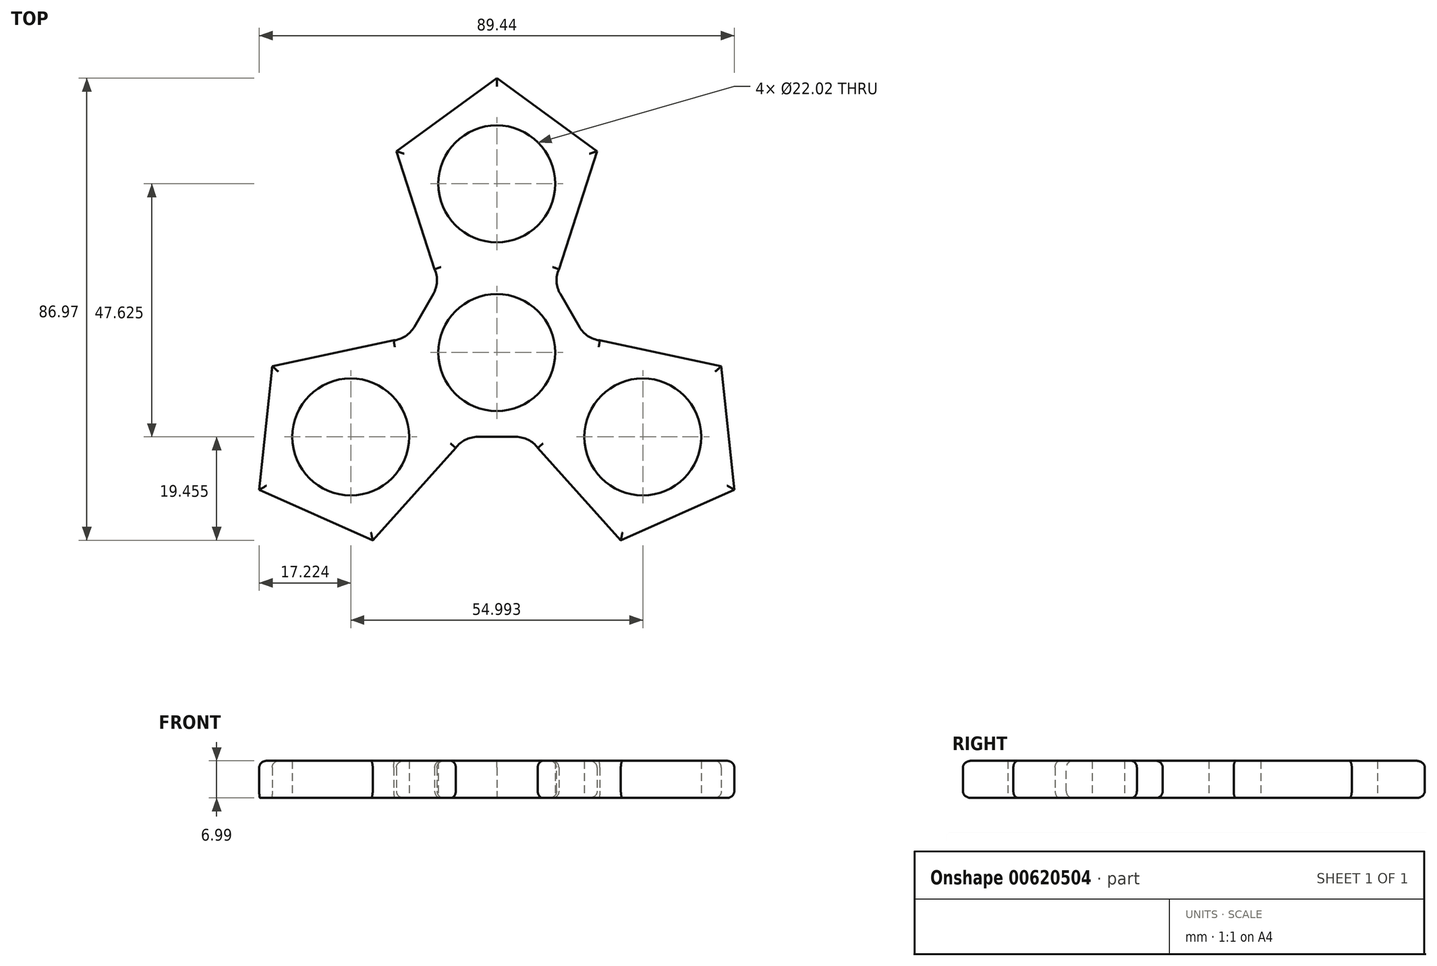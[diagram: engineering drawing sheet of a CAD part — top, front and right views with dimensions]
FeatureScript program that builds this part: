
annotation { "Feature Type Name" : "Feature", "Feature Type Description" : "" }
export const myFeature = defineFeature(function(context is Context, id is Id, definition is map)
    precondition{}
    {
        {
            var Q0;
            Q0=qCreatedBy(makeId("Top.planeOp"),FACE);
            var sketch = newSketch(context, id + "F0", { "sketchPlane" : qUnion([Q0])});
            skCircle(sketch, "E0", {"center": v(0, 0) * mm, "radius": 1.4 * mm});
            skCircle(sketch, "E1", {"center": v(0, 0) * mm, "radius": 11.01 * mm});
            skLineSegment(sketch, "E2", {"start": v(0, 0) * mm, "end": v(0, 31.75) * mm});
            skLineSegment(sketch, "E3", {"start": v(0, 0) * mm, "end": v(-27.5, -15.88) * mm});
            skLineSegment(sketch, "E4", {"start": v(0, 0) * mm, "end": v(27.5, -15.87) * mm});
            skCircle(sketch, "E5", {"center": v(0, 31.75) * mm, "radius": 11.01 * mm});
            skCircle(sketch, "E6", {"center": v(27.5, -15.87) * mm, "radius": 11.01 * mm});
            skCircle(sketch, "E7", {"center": v(-27.5, -15.88) * mm, "radius": 11.01 * mm});
            skCircle(sketch, "E8.cCircle", {"center": v(0, 31.75) * mm, "radius": 19.89 * mm, "construction": true});
            skLineSegment(sketch, "E8.0", {"start": v(0, 51.64) * mm, "end": v(18.92, 37.9) * mm});
            skLineSegment(sketch, "E8.1", {"start": v(18.92, 37.9) * mm, "end": v(11.7, 15.66) * mm});
            skLineSegment(sketch, "E8.2", {"start": v(11.7, 15.66) * mm, "end": v(-11.7, 15.66) * mm});
            skLineSegment(sketch, "E8.3", {"start": v(-11.7, 15.66) * mm, "end": v(-18.92, 37.9) * mm});
            skLineSegment(sketch, "E8.4", {"start": v(-18.92, 37.9) * mm, "end": v(0, 51.64) * mm});
            skCircle(sketch, "E9.cCircle", {"center": v(-27.5, -15.88) * mm, "radius": 19.89 * mm, "construction": true});
            skLineSegment(sketch, "E9.0", {"start": v(-19.4, 2.3) * mm, "end": v(-7.72, -17.95) * mm});
            skLineSegment(sketch, "E9.1", {"start": v(-7.72, -17.95) * mm, "end": v(-23.36, -35.33) * mm});
            skLineSegment(sketch, "E9.2", {"start": v(-23.36, -35.33) * mm, "end": v(-44.72, -25.82) * mm});
            skLineSegment(sketch, "E9.3", {"start": v(-44.72, -25.82) * mm, "end": v(-42.28, -2.57) * mm});
            skLineSegment(sketch, "E9.4", {"start": v(-42.28, -2.57) * mm, "end": v(-19.4, 2.3) * mm});
            skLineSegment(sketch, "E10", {"start": v(-27.5, -15.88) * mm, "end": v(0, 31.75) * mm});
            skLineSegment(sketch, "E11", {"start": v(0, 31.75) * mm, "end": v(27.5, -15.87) * mm});
            skLineSegment(sketch, "E12", {"start": v(27.5, -15.87) * mm, "end": v(-27.5, -15.88) * mm});
            skCircle(sketch, "E13.cCircle", {"center": v(27.5, -15.87) * mm, "radius": 19.89 * mm, "construction": true});
            skLineSegment(sketch, "E13.0", {"start": v(44.72, -25.82) * mm, "end": v(23.36, -35.33) * mm});
            skLineSegment(sketch, "E13.1", {"start": v(23.36, -35.33) * mm, "end": v(7.72, -17.95) * mm});
            skLineSegment(sketch, "E13.2", {"start": v(7.72, -17.95) * mm, "end": v(19.4, 2.3) * mm});
            skLineSegment(sketch, "E13.3", {"start": v(19.4, 2.3) * mm, "end": v(42.28, -2.57) * mm});
            skLineSegment(sketch, "E13.4", {"start": v(42.28, -2.57) * mm, "end": v(44.72, -25.82) * mm});
            skSolve(sketch);
        }
        {
            var Q0;
            Q0=makeQuery(id+"F0.imprint","IMPRINT",FACE,{"disambiguationData":[TD([[makeQuery(id+"F0.imprint","IMPRINT",EDGE,{"derivedFrom":sQuery(id+"F0.wireOp",EDGE,"E8.0")}),-1.0]])]});
            var Q1;
            {var subQ0=sQuery(id+"F0.wireOp",EDGE,"E8.2");var subQ1=sQuery(id+"F0.wireOp",EDGE,"E2");var subQ2=makeQuery(id+"F0.imprint","INTERSECT",VERTEX,{"derivedFrom":[subQ1,subQ0]});Q1=makeQuery(id+"F0.imprint","IMPRINT",FACE,{"disambiguationData":[TD([[makeQuery(id+"F0.imprint","IMPRINT",EDGE,{"disambiguationData":[TD([[subQ2,-1.0]])],"derivedFrom":subQ1}),-1.0]])]});}
            var Q2;
            {var subQ0=sQuery(id+"F0.wireOp",EDGE,"E8.2");var subQ1=sQuery(id+"F0.wireOp",EDGE,"E2");var subQ2=makeQuery(id+"F0.imprint","INTERSECT",VERTEX,{"derivedFrom":[subQ1,subQ0]});Q2=makeQuery(id+"F0.imprint","IMPRINT",FACE,{"disambiguationData":[TD([[makeQuery(id+"F0.imprint","IMPRINT",EDGE,{"disambiguationData":[TD([[subQ2,-1.0]])],"derivedFrom":subQ1}),1.0]])]});}
            var Q3;
            {var subQ1=sQuery(id+"F0.wireOp",EDGE,"E9.0");var subQ3=sQuery(id+"F0.wireOp",EDGE,"E1");var subQ4=makeQuery(id+"F0.imprint","INTERSECT",VERTEX,{"derivedFrom":[subQ3,subQ1]});Q3=makeQuery(id+"F0.imprint","IMPRINT",FACE,{"disambiguationData":[TD([[makeQuery(id+"F0.imprint","IMPRINT",EDGE,{"disambiguationData":[TD([[subQ4,1.0]])],"derivedFrom":subQ3}),-1.0]])]});}
            var Q4;
            {var subQ1=sQuery(id+"F0.wireOp",EDGE,"E9.0");var subQ3=sQuery(id+"F0.wireOp",EDGE,"E1");var subQ4=makeQuery(id+"F0.imprint","INTERSECT",VERTEX,{"derivedFrom":[subQ3,subQ1]});Q4=makeQuery(id+"F0.imprint","IMPRINT",FACE,{"disambiguationData":[TD([[makeQuery(id+"F0.imprint","IMPRINT",EDGE,{"disambiguationData":[TD([[subQ4,-1.0]])],"derivedFrom":subQ3}),-1.0]])]});}
            var Q5;
            {var subQ0=sQuery(id+"F0.wireOp",EDGE,"E9.2");Q5=makeQuery(id+"F0.imprint","IMPRINT",FACE,{"disambiguationData":[TD([[makeQuery(id+"F0.imprint","IMPRINT",EDGE,{"derivedFrom":subQ0}),-1.0]])]});}
            var Q6;
            {var subQ0=sQuery(id+"F0.wireOp",EDGE,"8ebc8318-1411-40da-9cb2-afa56d5b8b3e.0");Q6=makeQuery(id+"F0.imprint","IMPRINT",FACE,{"disambiguationData":[TD([[makeQuery(id+"F0.imprint","IMPRINT",EDGE,{"derivedFrom":subQ0}),-1.0]])]});}
            var Q7;
            {var subQ3=sQuery(id+"F0.wireOp",EDGE,"E2");var subQ10=sQuery(id+"F0.wireOp",EDGE,"E1");var subQ13=makeQuery(id+"F0.imprint","INTERSECT",VERTEX,{"derivedFrom":[subQ10,subQ3]});Q7=makeQuery(id+"F0.imprint","IMPRINT",FACE,{"disambiguationData":[TD([[makeQuery(id+"F0.imprint","IMPRINT",EDGE,{"disambiguationData":[TD([[subQ13,1.0]])],"derivedFrom":subQ10}),-1.0]])]});}
            var Q8;
            {var subQ3=sQuery(id+"F0.wireOp",EDGE,"E3");var subQ6=sQuery(id+"F0.wireOp",EDGE,"E1");var subQ10=makeQuery(id+"F0.imprint","INTERSECT",VERTEX,{"derivedFrom":[subQ6,subQ3]});Q8=makeQuery(id+"F0.imprint","IMPRINT",FACE,{"disambiguationData":[TD([[makeQuery(id+"F0.imprint","IMPRINT",EDGE,{"disambiguationData":[TD([[subQ10,-1.0]])],"derivedFrom":subQ6}),-1.0]])]});}
            var Q9;
            {var subQ0=sQuery(id+"F0.wireOp",EDGE,"E9.0");var subQ1=sQuery(id+"F0.wireOp",EDGE,"E3");var subQ2=makeQuery(id+"F0.imprint","INTERSECT",VERTEX,{"derivedFrom":[subQ1,subQ0]});Q9=makeQuery(id+"F0.imprint","IMPRINT",FACE,{"disambiguationData":[TD([[makeQuery(id+"F0.imprint","IMPRINT",EDGE,{"disambiguationData":[TD([[subQ2,-1.0]])],"derivedFrom":subQ1}),-1.0]])]});}
            var Q10;
            {var subQ0=sQuery(id+"F0.wireOp",EDGE,"E9.0");var subQ1=sQuery(id+"F0.wireOp",EDGE,"E3");var subQ2=makeQuery(id+"F0.imprint","INTERSECT",VERTEX,{"derivedFrom":[subQ1,subQ0]});Q10=makeQuery(id+"F0.imprint","IMPRINT",FACE,{"disambiguationData":[TD([[makeQuery(id+"F0.imprint","IMPRINT",EDGE,{"disambiguationData":[TD([[subQ2,-1.0]])],"derivedFrom":subQ1}),1.0]])]});}
            var Q11;
            {var subQ0=sQuery(id+"F0.wireOp",EDGE,"E13.2");var subQ1=sQuery(id+"F0.wireOp",EDGE,"E4");var subQ2=makeQuery(id+"F0.imprint","INTERSECT",VERTEX,{"derivedFrom":[subQ1,subQ0]});Q11=makeQuery(id+"F0.imprint","IMPRINT",FACE,{"disambiguationData":[TD([[makeQuery(id+"F0.imprint","IMPRINT",EDGE,{"disambiguationData":[TD([[subQ2,-1.0]])],"derivedFrom":subQ1}),-1.0]])]});}
            var Q12;
            {var subQ0=sQuery(id+"F0.wireOp",EDGE,"E13.2");var subQ1=sQuery(id+"F0.wireOp",EDGE,"E4");var subQ2=makeQuery(id+"F0.imprint","INTERSECT",VERTEX,{"derivedFrom":[subQ1,subQ0]});Q12=makeQuery(id+"F0.imprint","IMPRINT",FACE,{"disambiguationData":[TD([[makeQuery(id+"F0.imprint","IMPRINT",EDGE,{"disambiguationData":[TD([[subQ2,-1.0]])],"derivedFrom":subQ1}),1.0]])]});}
            var Q13;
            Q13=makeQuery(id+"F0.imprint","IMPRINT",FACE,{"disambiguationData":[TD([[makeQuery(id+"F0.imprint","IMPRINT",EDGE,{"derivedFrom":sQuery(id+"F0.wireOp",EDGE,"E13.0")}),-1.0]])]});
            extrude(context, id + "F1", {"entities" : qUnion([Q0, Q1, Q2, Q3, Q4, Q5, Q6, Q7, Q8, Q9, Q10, Q11, Q12, Q13]), "depth" : 7 * mm, "offsetDistance" : 25.4 * mm});
        }
        {
            var Q0;
            Q0=makeQuery(id+"F1.opExtrude","SWEPT_EDGE",EDGE,{"disambiguationData":[OSD([sQuery(id+"F0.wireOp",EDGE,"E8.2"),sQuery(id+"F0.wireOp",EDGE,"E10")])]});
            var Q1;
            Q1=makeQuery(id+"F1.opExtrude","SWEPT_EDGE",EDGE,{"disambiguationData":[OSD([sQuery(id+"F0.wireOp",EDGE,"E9.0"),sQuery(id+"F0.wireOp",EDGE,"E10")])]});
            var Q2;
            Q2=makeQuery(id+"F1.opExtrude","SWEPT_EDGE",EDGE,{"disambiguationData":[OSD([sQuery(id+"F0.wireOp",EDGE,"E9.0"),sQuery(id+"F0.wireOp",EDGE,"E12")])]});
            var Q3;
            Q3=makeQuery(id+"F1.opExtrude","SWEPT_EDGE",EDGE,{"disambiguationData":[OSD([sQuery(id+"F0.wireOp",EDGE,"E12"),sQuery(id+"F0.wireOp",EDGE,"E13.2")])]});
            var Q4;
            Q4=makeQuery(id+"F1.opExtrude","SWEPT_EDGE",EDGE,{"disambiguationData":[OSD([sQuery(id+"F0.wireOp",EDGE,"E11"),sQuery(id+"F0.wireOp",EDGE,"E13.2")])]});
            var Q5;
            Q5=makeQuery(id+"F1.opExtrude","SWEPT_EDGE",EDGE,{"disambiguationData":[OSD([sQuery(id+"F0.wireOp",EDGE,"E8.2"),sQuery(id+"F0.wireOp",EDGE,"E11")])]});
            fillet(context, id + "F2", {"entities" : qUnion([Q0, Q1, Q2, Q3, Q4, Q5]), "radius" : 5.08 * mm, "tangentPropagation" : true, "allowEdgeOverflow" : false});
        }
        {
            var Q0;
            Q0=makeQuery(id+"F1.opExtrude","CAP_EDGE",EDGE,{"disambiguationData":[OSD([sQuery(id+"F0.wireOp",EDGE,"E8.0")])],"isStart":false});
            var Q1;
            Q1=makeQuery(id+"F1.opExtrude","CAP_EDGE",EDGE,{"disambiguationData":[OSD([sQuery(id+"F0.wireOp",EDGE,"E8.1")])],"isStart":false});
            var Q2;
            Q2=makeQuery(id+"F1.opExtrude","CAP_EDGE",EDGE,{"disambiguationData":[OSD([sQuery(id+"F0.wireOp",EDGE,"E11")])],"isStart":false});
            var Q3;
            {var subQ0=sQuery(id+"F0.wireOp",EDGE,"E11");var subQ1=sQuery(id+"F0.wireOp",EDGE,"E8.2");Q3=makeQuery(id+"F2.opFillet","BLEND_EDGE",EDGE,{"blendedFrom":[makeQuery(id+"F1.opExtrude","SWEPT_EDGE",EDGE,{"disambiguationData":[OSD([subQ1,subQ0])]}),makeQuery(id+"F1.opExtrude","CAP_FACE",FACE,{"disambiguationData":[OSD([sQuery(id+"F0.wireOp",EDGE,"E1"),sQuery(id+"F0.wireOp",EDGE,"E5"),sQuery(id+"F0.wireOp",EDGE,"E6"),sQuery(id+"F0.wireOp",EDGE,"E7"),sQuery(id+"F0.wireOp",EDGE,"E8.0"),sQuery(id+"F0.wireOp",EDGE,"E8.1"),subQ1,sQuery(id+"F0.wireOp",EDGE,"E8.3"),sQuery(id+"F0.wireOp",EDGE,"E8.4"),sQuery(id+"F0.wireOp",EDGE,"E9.0"),sQuery(id+"F0.wireOp",EDGE,"E9.1"),sQuery(id+"F0.wireOp",EDGE,"E9.2"),sQuery(id+"F0.wireOp",EDGE,"E9.3"),sQuery(id+"F0.wireOp",EDGE,"E9.4"),sQuery(id+"F0.wireOp",EDGE,"E10"),subQ0,sQuery(id+"F0.wireOp",EDGE,"E12"),sQuery(id+"F0.wireOp",EDGE,"E13.0"),sQuery(id+"F0.wireOp",EDGE,"E13.1"),sQuery(id+"F0.wireOp",EDGE,"E13.2"),sQuery(id+"F0.wireOp",EDGE,"E13.3"),sQuery(id+"F0.wireOp",EDGE,"E13.4")])],"isStart":false})],"blendedInto":[makeQuery(id+"F1.opExtrude","CAP_FACE",FACE,{"disambiguationData":[OSD([sQuery(id+"F0.wireOp",EDGE,"E1"),sQuery(id+"F0.wireOp",EDGE,"E5"),sQuery(id+"F0.wireOp",EDGE,"E6"),sQuery(id+"F0.wireOp",EDGE,"E7"),sQuery(id+"F0.wireOp",EDGE,"E8.0"),sQuery(id+"F0.wireOp",EDGE,"E8.1"),subQ1,sQuery(id+"F0.wireOp",EDGE,"E8.3"),sQuery(id+"F0.wireOp",EDGE,"E8.4"),sQuery(id+"F0.wireOp",EDGE,"E9.0"),sQuery(id+"F0.wireOp",EDGE,"E9.1"),sQuery(id+"F0.wireOp",EDGE,"E9.2"),sQuery(id+"F0.wireOp",EDGE,"E9.3"),sQuery(id+"F0.wireOp",EDGE,"E9.4"),sQuery(id+"F0.wireOp",EDGE,"E10"),subQ0,sQuery(id+"F0.wireOp",EDGE,"E12"),sQuery(id+"F0.wireOp",EDGE,"E13.0"),sQuery(id+"F0.wireOp",EDGE,"E13.1"),sQuery(id+"F0.wireOp",EDGE,"E13.2"),sQuery(id+"F0.wireOp",EDGE,"E13.3"),sQuery(id+"F0.wireOp",EDGE,"E13.4")])],"isStart":false})]});}
            var Q4;
            {var subQ0=sQuery(id+"F0.wireOp",EDGE,"E13.2");var subQ1=sQuery(id+"F0.wireOp",EDGE,"E11");Q4=makeQuery(id+"F2.opFillet","BLEND_EDGE",EDGE,{"blendedFrom":[makeQuery(id+"F1.opExtrude","SWEPT_EDGE",EDGE,{"disambiguationData":[OSD([subQ1,subQ0])]}),makeQuery(id+"F1.opExtrude","CAP_FACE",FACE,{"disambiguationData":[OSD([sQuery(id+"F0.wireOp",EDGE,"E1"),sQuery(id+"F0.wireOp",EDGE,"E5"),sQuery(id+"F0.wireOp",EDGE,"E6"),sQuery(id+"F0.wireOp",EDGE,"E7"),sQuery(id+"F0.wireOp",EDGE,"E8.0"),sQuery(id+"F0.wireOp",EDGE,"E8.1"),sQuery(id+"F0.wireOp",EDGE,"E8.2"),sQuery(id+"F0.wireOp",EDGE,"E8.3"),sQuery(id+"F0.wireOp",EDGE,"E8.4"),sQuery(id+"F0.wireOp",EDGE,"E9.0"),sQuery(id+"F0.wireOp",EDGE,"E9.1"),sQuery(id+"F0.wireOp",EDGE,"E9.2"),sQuery(id+"F0.wireOp",EDGE,"E9.3"),sQuery(id+"F0.wireOp",EDGE,"E9.4"),sQuery(id+"F0.wireOp",EDGE,"E10"),subQ1,sQuery(id+"F0.wireOp",EDGE,"E12"),sQuery(id+"F0.wireOp",EDGE,"E13.0"),sQuery(id+"F0.wireOp",EDGE,"E13.1"),subQ0,sQuery(id+"F0.wireOp",EDGE,"E13.3"),sQuery(id+"F0.wireOp",EDGE,"E13.4")])],"isStart":false})],"blendedInto":[makeQuery(id+"F1.opExtrude","CAP_FACE",FACE,{"disambiguationData":[OSD([sQuery(id+"F0.wireOp",EDGE,"E1"),sQuery(id+"F0.wireOp",EDGE,"E5"),sQuery(id+"F0.wireOp",EDGE,"E6"),sQuery(id+"F0.wireOp",EDGE,"E7"),sQuery(id+"F0.wireOp",EDGE,"E8.0"),sQuery(id+"F0.wireOp",EDGE,"E8.1"),sQuery(id+"F0.wireOp",EDGE,"E8.2"),sQuery(id+"F0.wireOp",EDGE,"E8.3"),sQuery(id+"F0.wireOp",EDGE,"E8.4"),sQuery(id+"F0.wireOp",EDGE,"E9.0"),sQuery(id+"F0.wireOp",EDGE,"E9.1"),sQuery(id+"F0.wireOp",EDGE,"E9.2"),sQuery(id+"F0.wireOp",EDGE,"E9.3"),sQuery(id+"F0.wireOp",EDGE,"E9.4"),sQuery(id+"F0.wireOp",EDGE,"E10"),subQ1,sQuery(id+"F0.wireOp",EDGE,"E12"),sQuery(id+"F0.wireOp",EDGE,"E13.0"),sQuery(id+"F0.wireOp",EDGE,"E13.1"),subQ0,sQuery(id+"F0.wireOp",EDGE,"E13.3"),sQuery(id+"F0.wireOp",EDGE,"E13.4")])],"isStart":false})]});}
            var Q5;
            Q5=makeQuery(id+"F1.opExtrude","CAP_EDGE",EDGE,{"disambiguationData":[OSD([sQuery(id+"F0.wireOp",EDGE,"E13.3")])],"isStart":false});
            var Q6;
            Q6=makeQuery(id+"F1.opExtrude","CAP_EDGE",EDGE,{"disambiguationData":[OSD([sQuery(id+"F0.wireOp",EDGE,"E13.4")])],"isStart":false});
            var Q7;
            Q7=makeQuery(id+"F1.opExtrude","CAP_EDGE",EDGE,{"disambiguationData":[OSD([sQuery(id+"F0.wireOp",EDGE,"E13.0")])],"isStart":false});
            var Q8;
            Q8=makeQuery(id+"F1.opExtrude","CAP_EDGE",EDGE,{"disambiguationData":[OSD([sQuery(id+"F0.wireOp",EDGE,"E13.1")])],"isStart":false});
            var Q9;
            Q9=makeQuery(id+"F1.opExtrude","CAP_EDGE",EDGE,{"disambiguationData":[OSD([sQuery(id+"F0.wireOp",EDGE,"E12")])],"isStart":false});
            var Q10;
            {var subQ0=sQuery(id+"F0.wireOp",EDGE,"E12");var subQ1=sQuery(id+"F0.wireOp",EDGE,"E9.0");Q10=makeQuery(id+"F2.opFillet","BLEND_EDGE",EDGE,{"blendedFrom":[makeQuery(id+"F1.opExtrude","SWEPT_EDGE",EDGE,{"disambiguationData":[OSD([subQ1,subQ0])]}),makeQuery(id+"F1.opExtrude","CAP_FACE",FACE,{"disambiguationData":[OSD([sQuery(id+"F0.wireOp",EDGE,"E1"),sQuery(id+"F0.wireOp",EDGE,"E5"),sQuery(id+"F0.wireOp",EDGE,"E6"),sQuery(id+"F0.wireOp",EDGE,"E7"),sQuery(id+"F0.wireOp",EDGE,"E8.0"),sQuery(id+"F0.wireOp",EDGE,"E8.1"),sQuery(id+"F0.wireOp",EDGE,"E8.2"),sQuery(id+"F0.wireOp",EDGE,"E8.3"),sQuery(id+"F0.wireOp",EDGE,"E8.4"),subQ1,sQuery(id+"F0.wireOp",EDGE,"E9.1"),sQuery(id+"F0.wireOp",EDGE,"E9.2"),sQuery(id+"F0.wireOp",EDGE,"E9.3"),sQuery(id+"F0.wireOp",EDGE,"E9.4"),sQuery(id+"F0.wireOp",EDGE,"E10"),sQuery(id+"F0.wireOp",EDGE,"E11"),subQ0,sQuery(id+"F0.wireOp",EDGE,"E13.0"),sQuery(id+"F0.wireOp",EDGE,"E13.1"),sQuery(id+"F0.wireOp",EDGE,"E13.2"),sQuery(id+"F0.wireOp",EDGE,"E13.3"),sQuery(id+"F0.wireOp",EDGE,"E13.4")])],"isStart":false})],"blendedInto":[makeQuery(id+"F1.opExtrude","CAP_FACE",FACE,{"disambiguationData":[OSD([sQuery(id+"F0.wireOp",EDGE,"E1"),sQuery(id+"F0.wireOp",EDGE,"E5"),sQuery(id+"F0.wireOp",EDGE,"E6"),sQuery(id+"F0.wireOp",EDGE,"E7"),sQuery(id+"F0.wireOp",EDGE,"E8.0"),sQuery(id+"F0.wireOp",EDGE,"E8.1"),sQuery(id+"F0.wireOp",EDGE,"E8.2"),sQuery(id+"F0.wireOp",EDGE,"E8.3"),sQuery(id+"F0.wireOp",EDGE,"E8.4"),subQ1,sQuery(id+"F0.wireOp",EDGE,"E9.1"),sQuery(id+"F0.wireOp",EDGE,"E9.2"),sQuery(id+"F0.wireOp",EDGE,"E9.3"),sQuery(id+"F0.wireOp",EDGE,"E9.4"),sQuery(id+"F0.wireOp",EDGE,"E10"),sQuery(id+"F0.wireOp",EDGE,"E11"),subQ0,sQuery(id+"F0.wireOp",EDGE,"E13.0"),sQuery(id+"F0.wireOp",EDGE,"E13.1"),sQuery(id+"F0.wireOp",EDGE,"E13.2"),sQuery(id+"F0.wireOp",EDGE,"E13.3"),sQuery(id+"F0.wireOp",EDGE,"E13.4")])],"isStart":false})]});}
            var Q11;
            Q11=makeQuery(id+"F1.opExtrude","CAP_EDGE",EDGE,{"disambiguationData":[OSD([sQuery(id+"F0.wireOp",EDGE,"E9.1")])],"isStart":false});
            var Q12;
            Q12=makeQuery(id+"F1.opExtrude","CAP_EDGE",EDGE,{"disambiguationData":[OSD([sQuery(id+"F0.wireOp",EDGE,"E9.2")])],"isStart":false});
            var Q13;
            Q13=makeQuery(id+"F1.opExtrude","CAP_EDGE",EDGE,{"disambiguationData":[OSD([sQuery(id+"F0.wireOp",EDGE,"E9.3")])],"isStart":false});
            var Q14;
            Q14=makeQuery(id+"F1.opExtrude","CAP_EDGE",EDGE,{"disambiguationData":[OSD([sQuery(id+"F0.wireOp",EDGE,"E9.4")])],"isStart":false});
            var Q15;
            {var subQ0=sQuery(id+"F0.wireOp",EDGE,"E10");var subQ1=sQuery(id+"F0.wireOp",EDGE,"E9.0");Q15=makeQuery(id+"F2.opFillet","BLEND_EDGE",EDGE,{"blendedFrom":[makeQuery(id+"F1.opExtrude","SWEPT_EDGE",EDGE,{"disambiguationData":[OSD([subQ1,subQ0])]}),makeQuery(id+"F1.opExtrude","CAP_FACE",FACE,{"disambiguationData":[OSD([sQuery(id+"F0.wireOp",EDGE,"E1"),sQuery(id+"F0.wireOp",EDGE,"E5"),sQuery(id+"F0.wireOp",EDGE,"E6"),sQuery(id+"F0.wireOp",EDGE,"E7"),sQuery(id+"F0.wireOp",EDGE,"E8.0"),sQuery(id+"F0.wireOp",EDGE,"E8.1"),sQuery(id+"F0.wireOp",EDGE,"E8.2"),sQuery(id+"F0.wireOp",EDGE,"E8.3"),sQuery(id+"F0.wireOp",EDGE,"E8.4"),subQ1,sQuery(id+"F0.wireOp",EDGE,"E9.1"),sQuery(id+"F0.wireOp",EDGE,"E9.2"),sQuery(id+"F0.wireOp",EDGE,"E9.3"),sQuery(id+"F0.wireOp",EDGE,"E9.4"),subQ0,sQuery(id+"F0.wireOp",EDGE,"E11"),sQuery(id+"F0.wireOp",EDGE,"E12"),sQuery(id+"F0.wireOp",EDGE,"E13.0"),sQuery(id+"F0.wireOp",EDGE,"E13.1"),sQuery(id+"F0.wireOp",EDGE,"E13.2"),sQuery(id+"F0.wireOp",EDGE,"E13.3"),sQuery(id+"F0.wireOp",EDGE,"E13.4")])],"isStart":false})],"blendedInto":[makeQuery(id+"F1.opExtrude","CAP_FACE",FACE,{"disambiguationData":[OSD([sQuery(id+"F0.wireOp",EDGE,"E1"),sQuery(id+"F0.wireOp",EDGE,"E5"),sQuery(id+"F0.wireOp",EDGE,"E6"),sQuery(id+"F0.wireOp",EDGE,"E7"),sQuery(id+"F0.wireOp",EDGE,"E8.0"),sQuery(id+"F0.wireOp",EDGE,"E8.1"),sQuery(id+"F0.wireOp",EDGE,"E8.2"),sQuery(id+"F0.wireOp",EDGE,"E8.3"),sQuery(id+"F0.wireOp",EDGE,"E8.4"),subQ1,sQuery(id+"F0.wireOp",EDGE,"E9.1"),sQuery(id+"F0.wireOp",EDGE,"E9.2"),sQuery(id+"F0.wireOp",EDGE,"E9.3"),sQuery(id+"F0.wireOp",EDGE,"E9.4"),subQ0,sQuery(id+"F0.wireOp",EDGE,"E11"),sQuery(id+"F0.wireOp",EDGE,"E12"),sQuery(id+"F0.wireOp",EDGE,"E13.0"),sQuery(id+"F0.wireOp",EDGE,"E13.1"),sQuery(id+"F0.wireOp",EDGE,"E13.2"),sQuery(id+"F0.wireOp",EDGE,"E13.3"),sQuery(id+"F0.wireOp",EDGE,"E13.4")])],"isStart":false})]});}
            var Q16;
            Q16=makeQuery(id+"F1.opExtrude","CAP_EDGE",EDGE,{"disambiguationData":[OSD([sQuery(id+"F0.wireOp",EDGE,"E10")])],"isStart":false});
            var Q17;
            {var subQ0=sQuery(id+"F0.wireOp",EDGE,"E10");var subQ1=sQuery(id+"F0.wireOp",EDGE,"E8.2");Q17=makeQuery(id+"F2.opFillet","BLEND_EDGE",EDGE,{"blendedFrom":[makeQuery(id+"F1.opExtrude","SWEPT_EDGE",EDGE,{"disambiguationData":[OSD([subQ1,subQ0])]}),makeQuery(id+"F1.opExtrude","CAP_FACE",FACE,{"disambiguationData":[OSD([sQuery(id+"F0.wireOp",EDGE,"E1"),sQuery(id+"F0.wireOp",EDGE,"E5"),sQuery(id+"F0.wireOp",EDGE,"E6"),sQuery(id+"F0.wireOp",EDGE,"E7"),sQuery(id+"F0.wireOp",EDGE,"E8.0"),sQuery(id+"F0.wireOp",EDGE,"E8.1"),subQ1,sQuery(id+"F0.wireOp",EDGE,"E8.3"),sQuery(id+"F0.wireOp",EDGE,"E8.4"),sQuery(id+"F0.wireOp",EDGE,"E9.0"),sQuery(id+"F0.wireOp",EDGE,"E9.1"),sQuery(id+"F0.wireOp",EDGE,"E9.2"),sQuery(id+"F0.wireOp",EDGE,"E9.3"),sQuery(id+"F0.wireOp",EDGE,"E9.4"),subQ0,sQuery(id+"F0.wireOp",EDGE,"E11"),sQuery(id+"F0.wireOp",EDGE,"E12"),sQuery(id+"F0.wireOp",EDGE,"E13.0"),sQuery(id+"F0.wireOp",EDGE,"E13.1"),sQuery(id+"F0.wireOp",EDGE,"E13.2"),sQuery(id+"F0.wireOp",EDGE,"E13.3"),sQuery(id+"F0.wireOp",EDGE,"E13.4")])],"isStart":false})],"blendedInto":[makeQuery(id+"F1.opExtrude","CAP_FACE",FACE,{"disambiguationData":[OSD([sQuery(id+"F0.wireOp",EDGE,"E1"),sQuery(id+"F0.wireOp",EDGE,"E5"),sQuery(id+"F0.wireOp",EDGE,"E6"),sQuery(id+"F0.wireOp",EDGE,"E7"),sQuery(id+"F0.wireOp",EDGE,"E8.0"),sQuery(id+"F0.wireOp",EDGE,"E8.1"),subQ1,sQuery(id+"F0.wireOp",EDGE,"E8.3"),sQuery(id+"F0.wireOp",EDGE,"E8.4"),sQuery(id+"F0.wireOp",EDGE,"E9.0"),sQuery(id+"F0.wireOp",EDGE,"E9.1"),sQuery(id+"F0.wireOp",EDGE,"E9.2"),sQuery(id+"F0.wireOp",EDGE,"E9.3"),sQuery(id+"F0.wireOp",EDGE,"E9.4"),subQ0,sQuery(id+"F0.wireOp",EDGE,"E11"),sQuery(id+"F0.wireOp",EDGE,"E12"),sQuery(id+"F0.wireOp",EDGE,"E13.0"),sQuery(id+"F0.wireOp",EDGE,"E13.1"),sQuery(id+"F0.wireOp",EDGE,"E13.2"),sQuery(id+"F0.wireOp",EDGE,"E13.3"),sQuery(id+"F0.wireOp",EDGE,"E13.4")])],"isStart":false})]});}
            var Q18;
            Q18=makeQuery(id+"F1.opExtrude","CAP_EDGE",EDGE,{"disambiguationData":[OSD([sQuery(id+"F0.wireOp",EDGE,"E8.3")])],"isStart":false});
            var Q19;
            Q19=makeQuery(id+"F1.opExtrude","CAP_EDGE",EDGE,{"disambiguationData":[OSD([sQuery(id+"F0.wireOp",EDGE,"E8.4")])],"isStart":false});
            var Q20;
            {var subQ0=sQuery(id+"F0.wireOp",EDGE,"E13.2");var subQ1=sQuery(id+"F0.wireOp",EDGE,"E12");Q20=makeQuery(id+"F2.opFillet","BLEND_EDGE",EDGE,{"blendedFrom":[makeQuery(id+"F1.opExtrude","SWEPT_EDGE",EDGE,{"disambiguationData":[OSD([subQ1,subQ0])]}),makeQuery(id+"F1.opExtrude","CAP_FACE",FACE,{"disambiguationData":[OSD([sQuery(id+"F0.wireOp",EDGE,"E1"),sQuery(id+"F0.wireOp",EDGE,"E5"),sQuery(id+"F0.wireOp",EDGE,"E6"),sQuery(id+"F0.wireOp",EDGE,"E7"),sQuery(id+"F0.wireOp",EDGE,"E8.0"),sQuery(id+"F0.wireOp",EDGE,"E8.1"),sQuery(id+"F0.wireOp",EDGE,"E8.2"),sQuery(id+"F0.wireOp",EDGE,"E8.3"),sQuery(id+"F0.wireOp",EDGE,"E8.4"),sQuery(id+"F0.wireOp",EDGE,"E9.0"),sQuery(id+"F0.wireOp",EDGE,"E9.1"),sQuery(id+"F0.wireOp",EDGE,"E9.2"),sQuery(id+"F0.wireOp",EDGE,"E9.3"),sQuery(id+"F0.wireOp",EDGE,"E9.4"),sQuery(id+"F0.wireOp",EDGE,"E10"),sQuery(id+"F0.wireOp",EDGE,"E11"),subQ1,sQuery(id+"F0.wireOp",EDGE,"E13.0"),sQuery(id+"F0.wireOp",EDGE,"E13.1"),subQ0,sQuery(id+"F0.wireOp",EDGE,"E13.3"),sQuery(id+"F0.wireOp",EDGE,"E13.4")])],"isStart":false})],"blendedInto":[makeQuery(id+"F1.opExtrude","CAP_FACE",FACE,{"disambiguationData":[OSD([sQuery(id+"F0.wireOp",EDGE,"E1"),sQuery(id+"F0.wireOp",EDGE,"E5"),sQuery(id+"F0.wireOp",EDGE,"E6"),sQuery(id+"F0.wireOp",EDGE,"E7"),sQuery(id+"F0.wireOp",EDGE,"E8.0"),sQuery(id+"F0.wireOp",EDGE,"E8.1"),sQuery(id+"F0.wireOp",EDGE,"E8.2"),sQuery(id+"F0.wireOp",EDGE,"E8.3"),sQuery(id+"F0.wireOp",EDGE,"E8.4"),sQuery(id+"F0.wireOp",EDGE,"E9.0"),sQuery(id+"F0.wireOp",EDGE,"E9.1"),sQuery(id+"F0.wireOp",EDGE,"E9.2"),sQuery(id+"F0.wireOp",EDGE,"E9.3"),sQuery(id+"F0.wireOp",EDGE,"E9.4"),sQuery(id+"F0.wireOp",EDGE,"E10"),sQuery(id+"F0.wireOp",EDGE,"E11"),subQ1,sQuery(id+"F0.wireOp",EDGE,"E13.0"),sQuery(id+"F0.wireOp",EDGE,"E13.1"),subQ0,sQuery(id+"F0.wireOp",EDGE,"E13.3"),sQuery(id+"F0.wireOp",EDGE,"E13.4")])],"isStart":false})]});}
            fillet(context, id + "F3", {"entities" : qUnion([Q0, Q1, Q2, Q3, Q4, Q5, Q6, Q7, Q8, Q9, Q10, Q11, Q12, Q13, Q14, Q15, Q16, Q17, Q18, Q19, Q20]), "radius" : 1.27 * mm, "tangentPropagation" : true, "allowEdgeOverflow" : false});
        }
        {
            var Q0;
            Q0=makeQuery(id+"F1.opExtrude","CAP_EDGE",EDGE,{"disambiguationData":[OSD([sQuery(id+"F0.wireOp",EDGE,"E13.4")])],"isStart":true});
            var Q1;
            Q1=makeQuery(id+"F1.opExtrude","CAP_EDGE",EDGE,{"disambiguationData":[OSD([sQuery(id+"F0.wireOp",EDGE,"E13.0")])],"isStart":true});
            var Q2;
            Q2=makeQuery(id+"F1.opExtrude","CAP_EDGE",EDGE,{"disambiguationData":[OSD([sQuery(id+"F0.wireOp",EDGE,"E13.1")])],"isStart":true});
            var Q3;
            Q3=makeQuery(id+"F1.opExtrude","CAP_EDGE",EDGE,{"disambiguationData":[OSD([sQuery(id+"F0.wireOp",EDGE,"E13.3")])],"isStart":true});
            var Q4;
            Q4=makeQuery(id+"F1.opExtrude","CAP_EDGE",EDGE,{"disambiguationData":[OSD([sQuery(id+"F0.wireOp",EDGE,"E8.1")])],"isStart":true});
            var Q5;
            Q5=makeQuery(id+"F1.opExtrude","CAP_EDGE",EDGE,{"disambiguationData":[OSD([sQuery(id+"F0.wireOp",EDGE,"E8.0")])],"isStart":true});
            var Q6;
            Q6=makeQuery(id+"F1.opExtrude","CAP_EDGE",EDGE,{"disambiguationData":[OSD([sQuery(id+"F0.wireOp",EDGE,"E8.4")])],"isStart":true});
            var Q7;
            Q7=makeQuery(id+"F1.opExtrude","CAP_EDGE",EDGE,{"disambiguationData":[OSD([sQuery(id+"F0.wireOp",EDGE,"E8.3")])],"isStart":true});
            var Q8;
            Q8=makeQuery(id+"F1.opExtrude","CAP_EDGE",EDGE,{"disambiguationData":[OSD([sQuery(id+"F0.wireOp",EDGE,"E10")])],"isStart":true});
            var Q9;
            Q9=makeQuery(id+"F1.opExtrude","CAP_EDGE",EDGE,{"disambiguationData":[OSD([sQuery(id+"F0.wireOp",EDGE,"E9.4")])],"isStart":true});
            var Q10;
            Q10=makeQuery(id+"F1.opExtrude","CAP_EDGE",EDGE,{"disambiguationData":[OSD([sQuery(id+"F0.wireOp",EDGE,"E9.2")])],"isStart":true});
            var Q11;
            Q11=makeQuery(id+"F1.opExtrude","CAP_EDGE",EDGE,{"disambiguationData":[OSD([sQuery(id+"F0.wireOp",EDGE,"E9.1")])],"isStart":true});
            var Q12;
            Q12=makeQuery(id+"F1.opExtrude","CAP_EDGE",EDGE,{"disambiguationData":[OSD([sQuery(id+"F0.wireOp",EDGE,"E12")])],"isStart":true});
            var Q13;
            Q13=makeQuery(id+"F1.opExtrude","CAP_EDGE",EDGE,{"disambiguationData":[OSD([sQuery(id+"F0.wireOp",EDGE,"E11")])],"isStart":true});
            fillet(context, id + "F4", {"entities" : qUnion([Q0, Q1, Q2, Q3, Q4, Q5, Q6, Q7, Q8, Q9, Q10, Q11, Q12, Q13]), "radius" : 1.27 * mm, "tangentPropagation" : true, "allowEdgeOverflow" : false});
        }
    });
